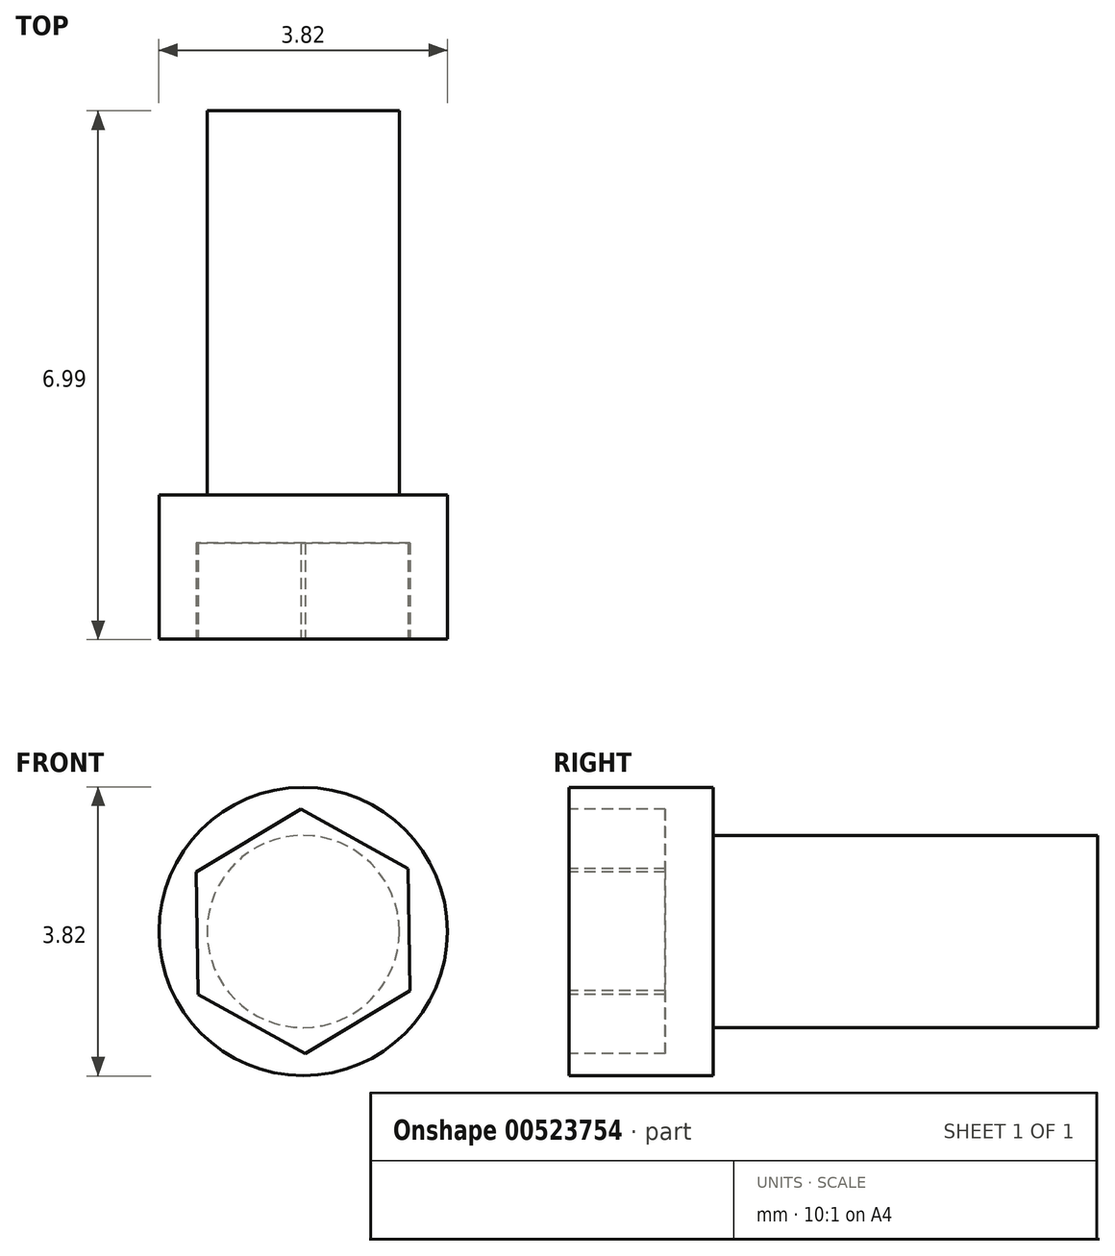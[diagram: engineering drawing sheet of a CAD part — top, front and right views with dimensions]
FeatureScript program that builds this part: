
annotation { "Feature Type Name" : "Feature", "Feature Type Description" : "" }
export const myFeature = defineFeature(function(context is Context, id is Id, definition is map)
    precondition{}
    {
        {
            var Q0;
            Q0=qCreatedBy(makeId("Front.planeOp"),FACE);
            var sketch = newSketch(context, id + "F0", { "sketchPlane" : qUnion([Q0])});
            skCircle(sketch, "E0", {"center": v(0, 0) * mm, "radius": 1.27 * mm});
            skSolve(sketch);
        }
        {
            var Q0;
            Q0=makeQuery(id+"F0.imprint","IMPRINT",FACE,{"disambiguationData":[TD([[makeQuery(id+"F0.imprint","IMPRINT",EDGE,{"derivedFrom":sQuery(id+"F0.wireOp",EDGE,"E0")}),1.0]])]});
            extrude(context, id + "F1", {"entities" : qUnion([Q0]), "depth" : 5.08 * mm, "offsetDistance" : 25.4 * mm});
        }
        {
            var Q0;
            Q0=makeQuery(id+"F1.opExtrude","CAP_FACE",FACE,{"disambiguationData":[OSD([sQuery(id+"F0.wireOp",EDGE,"E0")])],"isStart":false});
            var sketch = newSketch(context, id + "F2", { "sketchPlane" : qUnion([Q0])});
            skCircle(sketch, "E1", {"center": v(0, 0) * mm, "radius": 1.9 * mm});
            skSolve(sketch);
        }
        {
            var Q0;
            Q0=makeQuery(id+"F2.imprint","IMPRINT",FACE,{"disambiguationData":[TD([[makeQuery(id+"F2.imprint","IMPRINT",EDGE,{"derivedFrom":sQuery(id+"F2.wireOp",EDGE,"E1")}),1.0]])]});
            var Q1;
            Q1=makeQuery(id+"F2.imprint","IMPRINT",FACE,{"disambiguationData":[TD([[makeQuery(id+"F2.imprint","IMPRINT",EDGE,{"derivedFrom":makeQuery(id+"F1.opExtrude","CAP_EDGE",EDGE,{"disambiguationData":[OSD([sQuery(id+"F0.wireOp",EDGE,"E0")])],"isStart":false})}),1.0]])]});
            extrude(context, id + "F3", {"entities" : qUnion([Q0, Q1]), "operationType" : NewBodyOperationType.ADD, "depth" : 1.9 * mm, "offsetDistance" : 25.4 * mm});
        }
        {
            var Q0;
            Q0=makeQuery(id+"F3.opExtrude","CAP_FACE",FACE,{"disambiguationData":[OSD([sQuery(id+"F2.wireOp",EDGE,"E1")])],"isStart":false});
            var sketch = newSketch(context, id + "F4", { "sketchPlane" : qUnion([Q0])});
            skCircle(sketch, "E2.cCircle", {"center": v(0, 0) * mm, "radius": 1.4 * mm, "construction": true});
            skLineSegment(sketch, "E2.0", {"start": v(-0.03, 1.62) * mm, "end": v(1.39, 0.83) * mm});
            skLineSegment(sketch, "E2.1", {"start": v(1.39, 0.83) * mm, "end": v(1.41, -0.78) * mm});
            skLineSegment(sketch, "E2.2", {"start": v(1.41, -0.78) * mm, "end": v(0.03, -1.62) * mm});
            skLineSegment(sketch, "E2.3", {"start": v(0.03, -1.62) * mm, "end": v(-1.39, -0.83) * mm});
            skLineSegment(sketch, "E2.4", {"start": v(-1.39, -0.83) * mm, "end": v(-1.41, 0.78) * mm});
            skLineSegment(sketch, "E2.5", {"start": v(-1.41, 0.78) * mm, "end": v(-0.03, 1.62) * mm});
            skPoint(sketch, "E2.0.midPoint", {"position": v(0.68, 1.22) * mm});
            skSolve(sketch);
        }
        {
            var Q0;
            Q0=makeQuery(id+"F4.imprint","IMPRINT",FACE,{"disambiguationData":[TD([[makeQuery(id+"F4.imprint","IMPRINT",EDGE,{"derivedFrom":sQuery(id+"F4.wireOp",EDGE,"E2.0")}),-1.0]])]});
            extrude(context, id + "F5", {"entities" : qUnion([Q0]), "operationType" : NewBodyOperationType.REMOVE, "oppositeDirection" : true, "depth" : 1.27 * mm, "offsetDistance" : 25.4 * mm});
        }
    });
